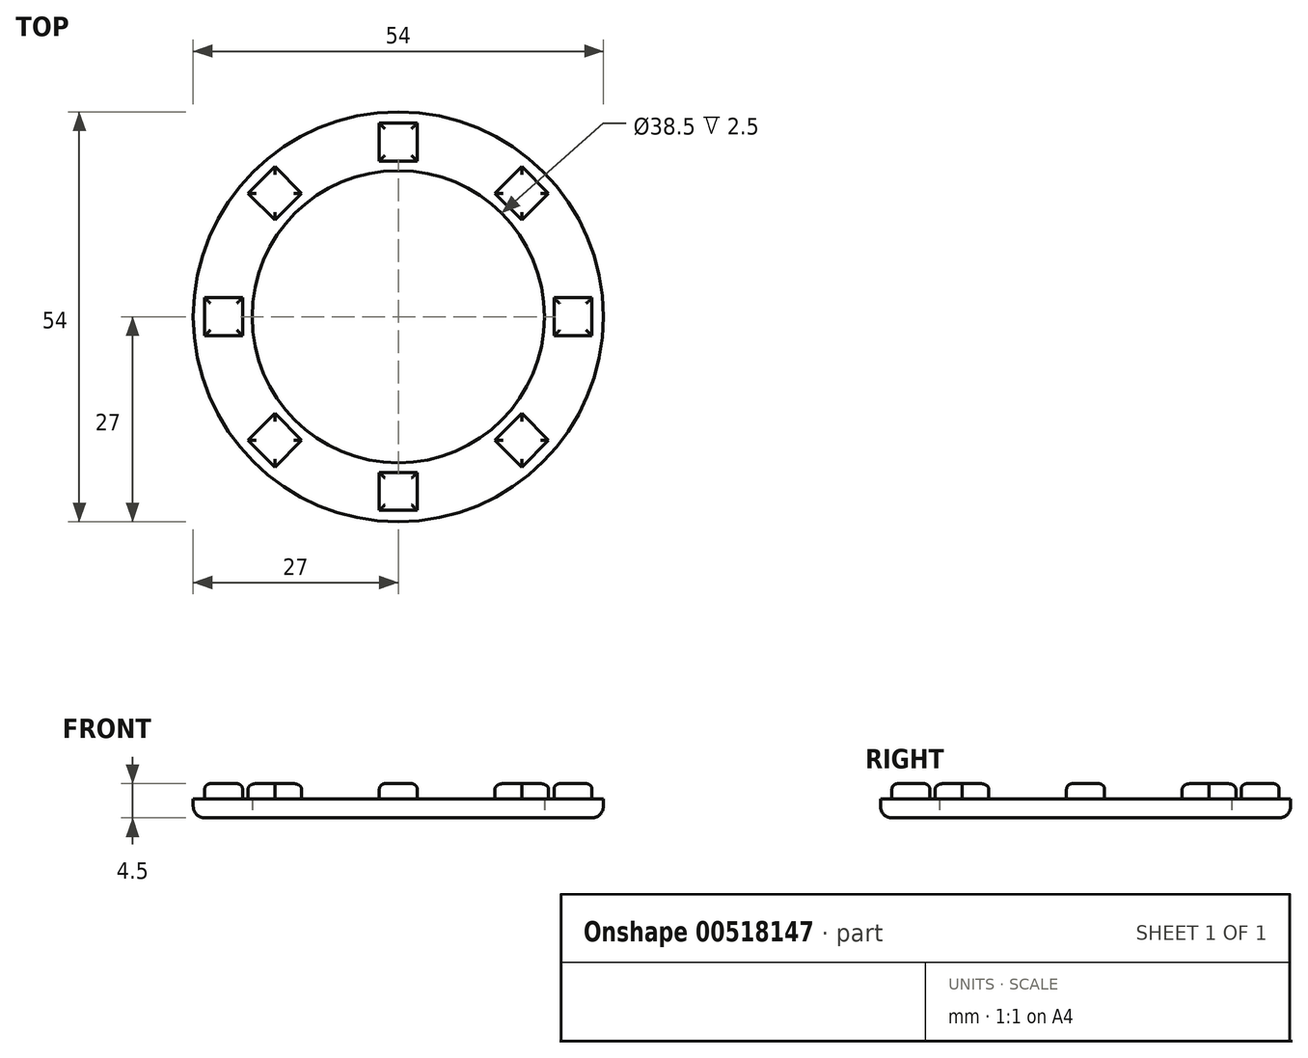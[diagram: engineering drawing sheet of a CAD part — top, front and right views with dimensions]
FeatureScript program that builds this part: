
annotation { "Feature Type Name" : "Feature", "Feature Type Description" : "" }
export const myFeature = defineFeature(function(context is Context, id is Id, definition is map)
    precondition{}
    {
        {
            var Q0;
            Q0=qCreatedBy(makeId("Top.planeOp"),FACE);
            var sketch = newSketch(context, id + "F0", { "sketchPlane" : qUnion([Q0])});
            skCircle(sketch, "E0", {"center": v(0, 0) * mm, "radius": 27 * mm});
            skCircle(sketch, "E1", {"center": v(0, 0) * mm, "radius": 19.25 * mm});
            skSolve(sketch);
        }
        {
            var Q0;
            Q0 = qSketchRegion(id + "F0", true);
            extrude(context, id + "F1", {"entities" : qUnion([Q0]), "depth" : 2.5 * mm, "offsetDistance" : 25 * mm});
        }
        {
            var Q0;
            Q0=makeQuery(id+"F1.opExtrude","CAP_FACE",FACE,{"disambiguationData":[OSD([sQuery(id+"F0.wireOp",EDGE,"E0"),sQuery(id+"F0.wireOp",EDGE,"E1")])],"isStart":false});
            var sketch = newSketch(context, id + "F2", { "sketchPlane" : qUnion([Q0])});
            skLineSegment(sketch, "E2", {"start": v(0, 0) * mm, "end": v(23, 0) * mm, "construction": true});
            skLineSegment(sketch, "E3.bottom", {"start": v(25.5, -2.5) * mm, "end": v(20.5, -2.5) * mm});
            skLineSegment(sketch, "E3.top", {"start": v(25.5, 2.5) * mm, "end": v(20.5, 2.5) * mm});
            skLineSegment(sketch, "E3.left", {"start": v(25.5, -2.5) * mm, "end": v(25.5, 2.5) * mm});
            skLineSegment(sketch, "E3.right", {"start": v(20.5, -2.5) * mm, "end": v(20.5, 2.5) * mm});
            skPoint(sketch, "E3.middle", {"position": v(23, 0) * mm});
            skLineSegment(sketch, "E4.1.0", {"start": v(16.26, 19.8) * mm, "end": v(12.73, 16.26) * mm});
            skLineSegment(sketch, "E4.1.1", {"start": v(19.8, 16.26) * mm, "end": v(16.26, 19.8) * mm});
            skLineSegment(sketch, "E4.1.2", {"start": v(16.26, 12.73) * mm, "end": v(12.73, 16.26) * mm});
            skLineSegment(sketch, "E4.1.3", {"start": v(19.8, 16.26) * mm, "end": v(16.26, 12.73) * mm});
            skLineSegment(sketch, "E4.2.0", {"start": v(-2.5, 25.5) * mm, "end": v(-2.5, 20.5) * mm});
            skLineSegment(sketch, "E4.2.1", {"start": v(2.5, 25.5) * mm, "end": v(-2.5, 25.5) * mm});
            skLineSegment(sketch, "E4.2.2", {"start": v(2.5, 20.5) * mm, "end": v(-2.5, 20.5) * mm});
            skLineSegment(sketch, "E4.2.3", {"start": v(2.5, 25.5) * mm, "end": v(2.5, 20.5) * mm});
            skLineSegment(sketch, "E4.3.0", {"start": v(-19.8, 16.26) * mm, "end": v(-16.26, 12.73) * mm});
            skLineSegment(sketch, "E4.3.1", {"start": v(-16.26, 19.8) * mm, "end": v(-19.8, 16.26) * mm});
            skLineSegment(sketch, "E4.3.2", {"start": v(-12.73, 16.26) * mm, "end": v(-16.26, 12.73) * mm});
            skLineSegment(sketch, "E4.3.3", {"start": v(-16.26, 19.8) * mm, "end": v(-12.73, 16.26) * mm});
            skLineSegment(sketch, "E4.4.0", {"start": v(-25.5, -2.5) * mm, "end": v(-20.5, -2.5) * mm});
            skLineSegment(sketch, "E4.4.1", {"start": v(-25.5, 2.5) * mm, "end": v(-25.5, -2.5) * mm});
            skLineSegment(sketch, "E4.4.2", {"start": v(-20.5, 2.5) * mm, "end": v(-20.5, -2.5) * mm});
            skLineSegment(sketch, "E4.4.3", {"start": v(-25.5, 2.5) * mm, "end": v(-20.5, 2.5) * mm});
            skLineSegment(sketch, "E4.5.0", {"start": v(-16.26, -19.8) * mm, "end": v(-12.73, -16.26) * mm});
            skLineSegment(sketch, "E4.5.1", {"start": v(-19.8, -16.26) * mm, "end": v(-16.26, -19.8) * mm});
            skLineSegment(sketch, "E4.5.2", {"start": v(-16.26, -12.73) * mm, "end": v(-12.73, -16.26) * mm});
            skLineSegment(sketch, "E4.5.3", {"start": v(-19.8, -16.26) * mm, "end": v(-16.26, -12.73) * mm});
            skLineSegment(sketch, "E4.6.0", {"start": v(2.5, -25.5) * mm, "end": v(2.5, -20.5) * mm});
            skLineSegment(sketch, "E4.6.1", {"start": v(-2.5, -25.5) * mm, "end": v(2.5, -25.5) * mm});
            skLineSegment(sketch, "E4.6.2", {"start": v(-2.5, -20.5) * mm, "end": v(2.5, -20.5) * mm});
            skLineSegment(sketch, "E4.6.3", {"start": v(-2.5, -25.5) * mm, "end": v(-2.5, -20.5) * mm});
            skLineSegment(sketch, "E4.7.0", {"start": v(19.8, -16.26) * mm, "end": v(16.26, -12.73) * mm});
            skLineSegment(sketch, "E4.7.1", {"start": v(16.26, -19.8) * mm, "end": v(19.8, -16.26) * mm});
            skLineSegment(sketch, "E4.7.2", {"start": v(12.73, -16.26) * mm, "end": v(16.26, -12.73) * mm});
            skLineSegment(sketch, "E4.7.3", {"start": v(16.26, -19.8) * mm, "end": v(12.73, -16.26) * mm});
            skPoint(sketch, "E4.center", {"position": v(0, 0) * mm});
            skSolve(sketch);
        }
        {
            var Q0;
            Q0 = qSketchRegion(id + "F2", true);
            extrude(context, id + "F3", {"entities" : qUnion([Q0]), "operationType" : NewBodyOperationType.ADD, "depth" : 2 * mm, "offsetDistance" : 25 * mm});
        }
        {
            var Q0;
            Q0=makeQuery(id+"F3.opExtrude","CAP_FACE",FACE,{"disambiguationData":[OSD([sQuery(id+"F2.wireOp",EDGE,"E4.4.0"),sQuery(id+"F2.wireOp",EDGE,"E4.4.1"),sQuery(id+"F2.wireOp",EDGE,"E4.4.2"),sQuery(id+"F2.wireOp",EDGE,"E4.4.3")])],"isStart":false});
            var Q1;
            Q1=makeQuery(id+"F3.opExtrude","CAP_FACE",FACE,{"disambiguationData":[OSD([sQuery(id+"F2.wireOp",EDGE,"E4.3.0"),sQuery(id+"F2.wireOp",EDGE,"E4.3.1"),sQuery(id+"F2.wireOp",EDGE,"E4.3.2"),sQuery(id+"F2.wireOp",EDGE,"E4.3.3")])],"isStart":false});
            var Q2;
            Q2=makeQuery(id+"F3.opExtrude","CAP_FACE",FACE,{"disambiguationData":[OSD([sQuery(id+"F2.wireOp",EDGE,"E4.2.0"),sQuery(id+"F2.wireOp",EDGE,"E4.2.1"),sQuery(id+"F2.wireOp",EDGE,"E4.2.2"),sQuery(id+"F2.wireOp",EDGE,"E4.2.3")])],"isStart":false});
            var Q3;
            Q3=makeQuery(id+"F3.opExtrude","CAP_FACE",FACE,{"disambiguationData":[OSD([sQuery(id+"F2.wireOp",EDGE,"E4.1.0"),sQuery(id+"F2.wireOp",EDGE,"E4.1.1"),sQuery(id+"F2.wireOp",EDGE,"E4.1.2"),sQuery(id+"F2.wireOp",EDGE,"E4.1.3")])],"isStart":false});
            var Q4;
            Q4=makeQuery(id+"F3.opExtrude","CAP_FACE",FACE,{"disambiguationData":[OSD([sQuery(id+"F2.wireOp",EDGE,"E3.bottom"),sQuery(id+"F2.wireOp",EDGE,"E3.top"),sQuery(id+"F2.wireOp",EDGE,"E3.left"),sQuery(id+"F2.wireOp",EDGE,"E3.right")])],"isStart":false});
            var Q5;
            Q5=makeQuery(id+"F3.opExtrude","CAP_FACE",FACE,{"disambiguationData":[OSD([sQuery(id+"F2.wireOp",EDGE,"E4.7.0"),sQuery(id+"F2.wireOp",EDGE,"E4.7.1"),sQuery(id+"F2.wireOp",EDGE,"E4.7.2"),sQuery(id+"F2.wireOp",EDGE,"E4.7.3")])],"isStart":false});
            var Q6;
            Q6=makeQuery(id+"F3.opExtrude","CAP_FACE",FACE,{"disambiguationData":[OSD([sQuery(id+"F2.wireOp",EDGE,"E4.6.0"),sQuery(id+"F2.wireOp",EDGE,"E4.6.1"),sQuery(id+"F2.wireOp",EDGE,"E4.6.2"),sQuery(id+"F2.wireOp",EDGE,"E4.6.3")])],"isStart":false});
            var Q7;
            Q7=makeQuery(id+"F3.opExtrude","CAP_FACE",FACE,{"disambiguationData":[OSD([sQuery(id+"F2.wireOp",EDGE,"E4.5.0"),sQuery(id+"F2.wireOp",EDGE,"E4.5.1"),sQuery(id+"F2.wireOp",EDGE,"E4.5.2"),sQuery(id+"F2.wireOp",EDGE,"E4.5.3")])],"isStart":false});
            fillet(context, id + "F4", {"entities" : qUnion([Q0, Q1, Q2, Q3, Q4, Q5, Q6, Q7]), "radius" : 0.75 * mm, "tangentPropagation" : true, "allowEdgeOverflow" : false});
        }
        {
            var Q0;
            Q0=makeQuery(id+"F1.opExtrude","CAP_EDGE",EDGE,{"disambiguationData":[OSD([sQuery(id+"F0.wireOp",EDGE,"E0")])],"isStart":true});
            fillet(context, id + "F5", {"entities" : qUnion([Q0]), "radius" : 1.5 * mm, "tangentPropagation" : true, "allowEdgeOverflow" : false});
        }
    });
